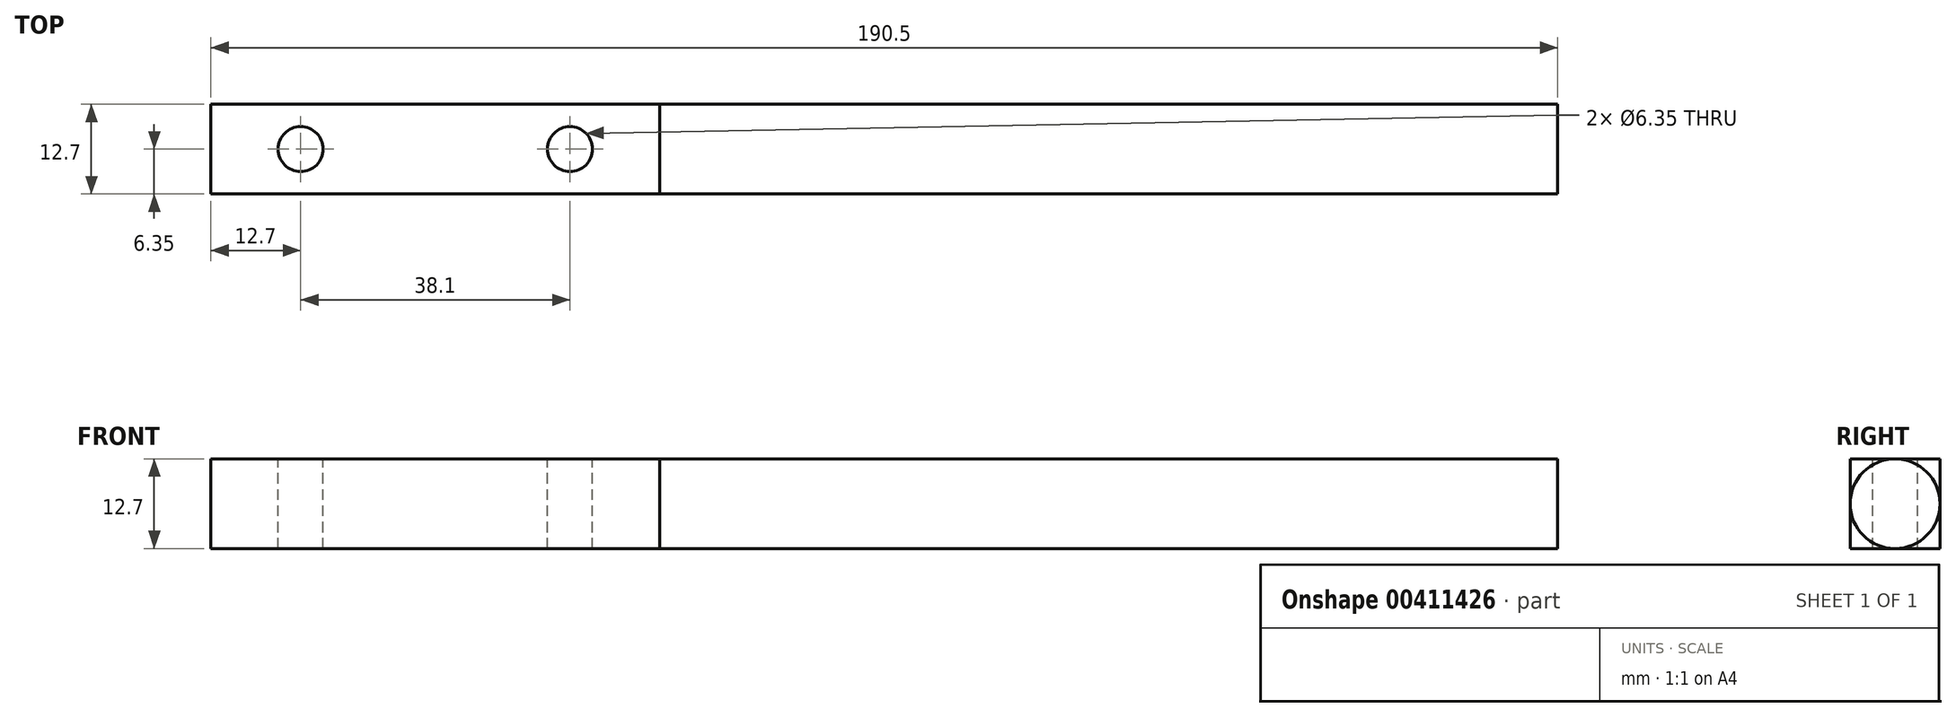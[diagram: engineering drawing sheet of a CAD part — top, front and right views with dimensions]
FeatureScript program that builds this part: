
annotation { "Feature Type Name" : "Feature", "Feature Type Description" : "" }
export const myFeature = defineFeature(function(context is Context, id is Id, definition is map)
    precondition{}
    {
        {
            var Q0;
            Q0=qCreatedBy(makeId("Right.planeOp"),FACE);
            var sketch = newSketch(context, id + "F0", { "sketchPlane" : qUnion([Q0])});
            skLineSegment(sketch, "E0.bottom", {"start": v(6.35, 6.35) * mm, "end": v(-6.35, 6.35) * mm});
            skLineSegment(sketch, "E0.top", {"start": v(6.35, -6.35) * mm, "end": v(-6.35, -6.35) * mm});
            skLineSegment(sketch, "E0.left", {"start": v(6.35, 6.35) * mm, "end": v(6.35, -6.35) * mm});
            skLineSegment(sketch, "E0.right", {"start": v(-6.35, 6.35) * mm, "end": v(-6.35, -6.35) * mm});
            skPoint(sketch, "E0.middle", {"position": v(0, 0) * mm});
            skSolve(sketch);
        }
        {
            var Q0;
            Q0 = qSketchRegion(id + "F0", true);
            extrude(context, id + "F1", {"entities" : qUnion([Q0]), "depth" : 63.5 * mm});
        }
        {
            var Q0;
            Q0=makeQuery(id+"F1.opExtrude","CAP_FACE",FACE,{"disambiguationData":[OSD([sQuery(id+"F0.wireOp",EDGE,"E0.bottom"),sQuery(id+"F0.wireOp",EDGE,"E0.top"),sQuery(id+"F0.wireOp",EDGE,"E0.left"),sQuery(id+"F0.wireOp",EDGE,"E0.right")])],"isStart":false});
            var sketch = newSketch(context, id + "F2", { "sketchPlane" : qUnion([Q0])});
            skCircle(sketch, "E1", {"center": v(0, 0) * mm, "radius": 6.35 * mm});
            skSolve(sketch);
        }
        {
            var Q0;
            Q0 = qSketchRegion(id + "F2", true);
            extrude(context, id + "F3", {"entities" : qUnion([Q0]), "operationType" : NewBodyOperationType.ADD, "depth" : 127 * mm});
        }
        {
            var Q0;
            Q0=makeQuery(id+"F1.opExtrude","SWEPT_FACE",FACE,{"disambiguationData":[OSD([sQuery(id+"F0.wireOp",EDGE,"E0.bottom")])]});
            var sketch = newSketch(context, id + "F4", { "sketchPlane" : qUnion([Q0])});
            skCircle(sketch, "E2", {"center": v(12.7, 0) * mm, "radius": 3.18 * mm});
            skCircle(sketch, "E3", {"center": v(50.8, 0) * mm, "radius": 3.18 * mm});
            skSolve(sketch);
        }
        {
            var Q0;
            Q0=sQuery(id+"F4.wireOp",VERTEX,"E2.center");
            var Q1;
            Q1=sQuery(id+"F4.wireOp",VERTEX,"E3.center");
            var Q2;
            Q2=makeQuery(id+"F1.opExtrude","SWEPT_BODY",BODY,{"disambiguationData":[OSD([sQuery(id+"F0.wireOp",EDGE,"E0.bottom"),sQuery(id+"F0.wireOp",EDGE,"E0.top"),sQuery(id+"F0.wireOp",EDGE,"E0.left"),sQuery(id+"F0.wireOp",EDGE,"E0.right")])]});
            hole(context, id + "F5", {"style" : HoleStyle.SIMPLE, "endStyle" : HoleEndStyle.THROUGH, "holeDiameter" : 6.35 * mm, "isTappedThrough" : true, "tappedDepth" : 12.7 * mm, "tapClearance" : 3, "locations" : qUnion([Q0, Q1]), "scope" : qUnion([Q2])});
        }
    });
